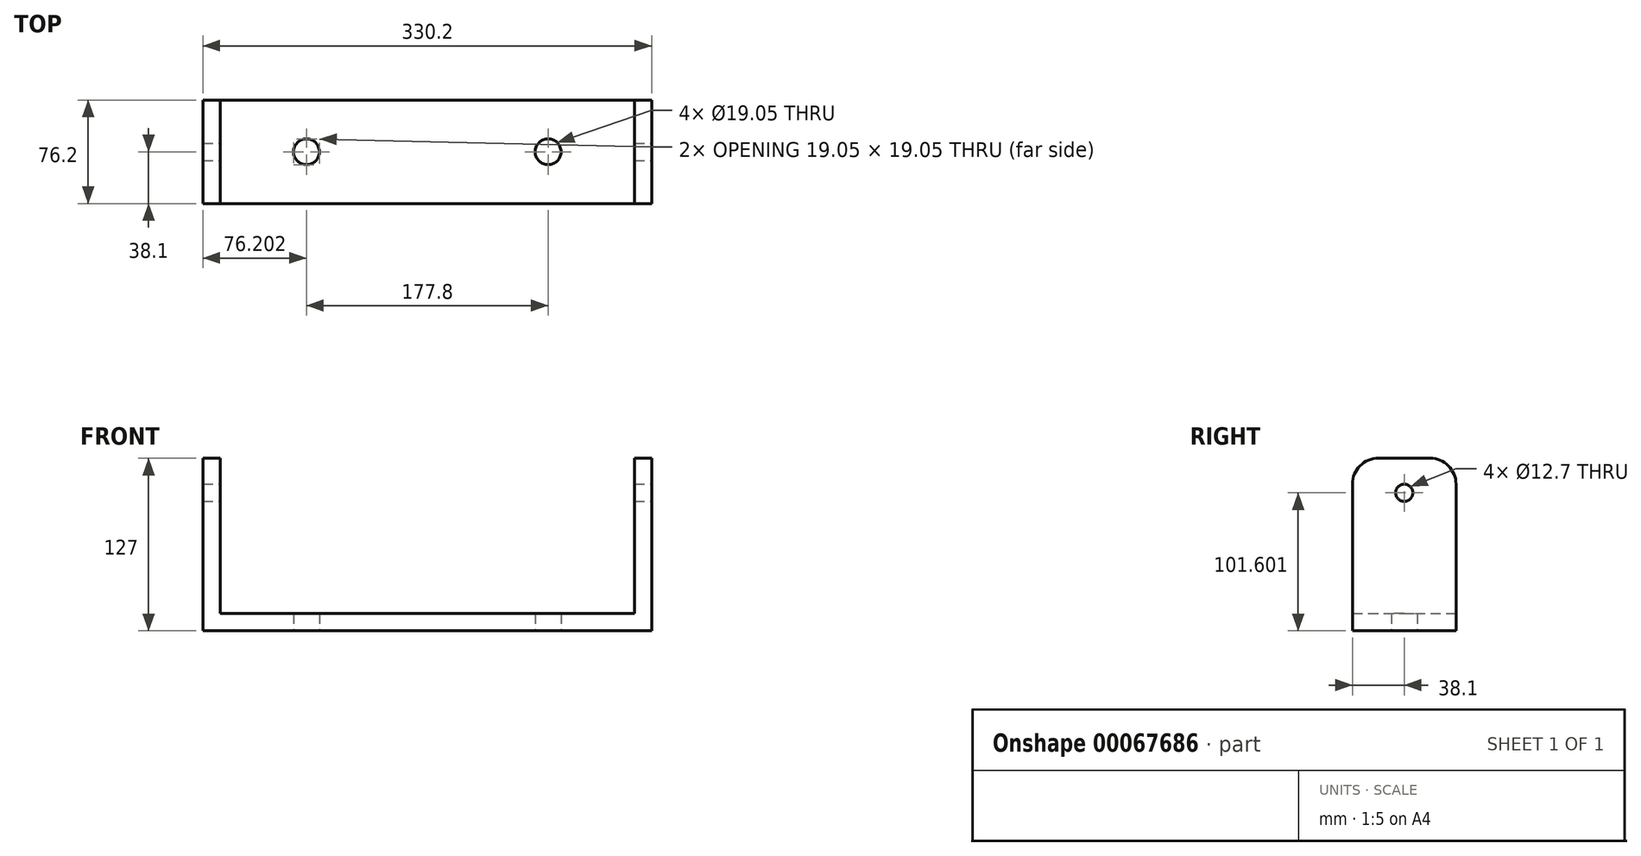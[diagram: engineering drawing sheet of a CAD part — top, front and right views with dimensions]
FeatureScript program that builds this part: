
annotation { "Feature Type Name" : "Feature", "Feature Type Description" : "" }
export const myFeature = defineFeature(function(context is Context, id is Id, definition is map)
    precondition{}
    {
        {
            var Q0;
            Q0=qCreatedBy(makeId("Front.planeOp"),FACE);
            var sketch = newSketch(context, id + "F0", { "sketchPlane" : qUnion([Q0])});
            skLineSegment(sketch, "E0.bottom", {"start": v(-115.73, 44.46) * mm, "end": v(-103.03, 44.46) * mm});
            skLineSegment(sketch, "E0.top", {"start": v(-115.73, -82.54) * mm, "end": v(214.47, -82.54) * mm});
            skLineSegment(sketch, "E0.left", {"start": v(-115.73, 44.46) * mm, "end": v(-115.73, -82.54) * mm});
            skLineSegment(sketch, "E0.right", {"start": v(214.47, 44.46) * mm, "end": v(214.47, -82.54) * mm});
            skLineSegment(sketch, "E1.top", {"start": v(-103.03, -69.84) * mm, "end": v(201.77, -69.84) * mm});
            skLineSegment(sketch, "E1.left", {"start": v(-103.03, 44.46) * mm, "end": v(-103.03, -69.84) * mm});
            skLineSegment(sketch, "E1.right", {"start": v(201.77, 44.46) * mm, "end": v(201.77, -69.84) * mm});
            skLineSegment(sketch, "E2.trimOffspring", {"start": v(201.77, 44.46) * mm, "end": v(214.47, 44.46) * mm});
            skSolve(sketch);
        }
        {
            var Q0;
            Q0=makeQuery(id+"F0.imprint","IMPRINT",FACE,{"disambiguationData":[TD([[makeQuery(id+"F0.imprint","IMPRINT",EDGE,{"derivedFrom":sQuery(id+"F0.wireOp",EDGE,"E0.bottom")}),-1.0]])]});
            extrude(context, id + "F1", {"entities" : qUnion([Q0]), "depth" : 76.2 * mm});
        }
        {
            var Q0;
            Q0=makeQuery(id+"F1.opExtrude","SWEPT_FACE",FACE,{"disambiguationData":[OSD([sQuery(id+"F0.wireOp",EDGE,"E0.right")])]});
            var sketch = newSketch(context, id + "F2", { "sketchPlane" : qUnion([Q0])});
            skPoint(sketch, "E3", {"position": v(-38.1, 19.06) * mm});
            skSolve(sketch);
        }
        {
            var Q0;
            Q0=sQuery(id+"F2.wireOp",VERTEX,"E3");
            var Q1;
            Q1=makeQuery(id+"F1.opExtrude","SWEPT_BODY",BODY,{"disambiguationData":[OSD([sQuery(id+"F0.wireOp",EDGE,"E0.bottom"),sQuery(id+"F0.wireOp",EDGE,"E0.top"),sQuery(id+"F0.wireOp",EDGE,"E0.left"),sQuery(id+"F0.wireOp",EDGE,"E0.right"),sQuery(id+"F0.wireOp",EDGE,"E1.top"),sQuery(id+"F0.wireOp",EDGE,"E1.left"),sQuery(id+"F0.wireOp",EDGE,"E1.right"),sQuery(id+"F0.wireOp",EDGE,"E2.trimOffspring")])]});
            hole(context, id + "F3", {"style" : HoleStyle.SIMPLE, "holeDiameter" : 12.7 * mm, "endStyle" : HoleEndStyle.THROUGH, "locations" : qUnion([Q0]), "scope" : qUnion([Q1])});
        }
        {
            var Q0;
            Q0=makeQuery(id+"F1.opExtrude","CAP_EDGE",EDGE,{"disambiguationData":[OSD([sQuery(id+"F0.wireOp",EDGE,"E2.trimOffspring")])],"isStart":false});
            var Q1;
            Q1=makeQuery(id+"F1.opExtrude","CAP_EDGE",EDGE,{"disambiguationData":[OSD([sQuery(id+"F0.wireOp",EDGE,"E2.trimOffspring")])],"isStart":true});
            var Q2;
            Q2=makeQuery(id+"F1.opExtrude","CAP_EDGE",EDGE,{"disambiguationData":[OSD([sQuery(id+"F0.wireOp",EDGE,"E0.bottom")])],"isStart":false});
            var Q3;
            Q3=makeQuery(id+"F1.opExtrude","CAP_EDGE",EDGE,{"disambiguationData":[OSD([sQuery(id+"F0.wireOp",EDGE,"E0.bottom")])],"isStart":true});
            fillet(context, id + "F4", {"entities" : qUnion([Q0, Q1, Q2, Q3]), "radius" : 19.05 * mm, "tangentPropagation" : true, "allowEdgeOverflow" : false});
        }
        {
            var Q0;
            Q0=makeQuery(id+"F1.opExtrude","SWEPT_FACE",FACE,{"disambiguationData":[OSD([sQuery(id+"F0.wireOp",EDGE,"E0.top")])]});
            var sketch = newSketch(context, id + "F5", { "sketchPlane" : qUnion([Q0])});
            skPoint(sketch, "E4", {"position": v(-39.53, 38.1) * mm});
            skPoint(sketch, "E5", {"position": v(138.27, 38.1) * mm});
            skSolve(sketch);
        }
        {
            var Q0;
            Q0=sQuery(id+"F5.wireOp",VERTEX,"E4");
            var Q1;
            Q1=sQuery(id+"F5.wireOp",VERTEX,"E5");
            var Q2;
            Q2=makeQuery(id+"F1.opExtrude","SWEPT_BODY",BODY,{"disambiguationData":[OSD([sQuery(id+"F0.wireOp",EDGE,"E0.bottom"),sQuery(id+"F0.wireOp",EDGE,"E0.top"),sQuery(id+"F0.wireOp",EDGE,"E0.left"),sQuery(id+"F0.wireOp",EDGE,"E0.right"),sQuery(id+"F0.wireOp",EDGE,"E1.top"),sQuery(id+"F0.wireOp",EDGE,"E1.left"),sQuery(id+"F0.wireOp",EDGE,"E1.right"),sQuery(id+"F0.wireOp",EDGE,"E2.trimOffspring")])]});
            hole(context, id + "F6", {"style" : HoleStyle.SIMPLE, "holeDiameter" : 19.05 * mm, "endStyle" : HoleEndStyle.THROUGH, "locations" : qUnion([Q0, Q1]), "scope" : qUnion([Q2])});
        }
    });
